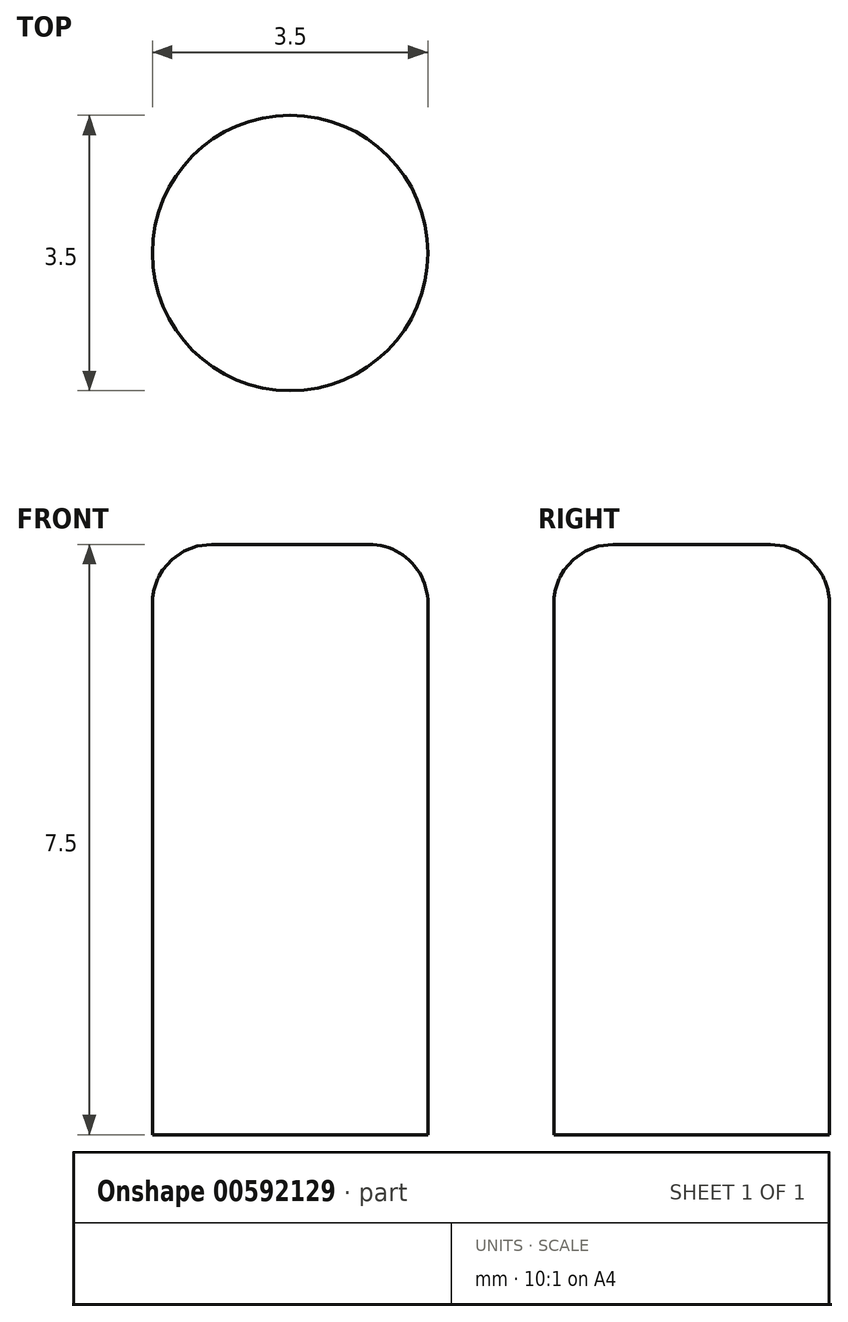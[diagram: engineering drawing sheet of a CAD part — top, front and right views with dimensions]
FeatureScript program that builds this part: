
annotation { "Feature Type Name" : "Feature", "Feature Type Description" : "" }
export const myFeature = defineFeature(function(context is Context, id is Id, definition is map)
    precondition{}
    {
        {
            var Q0;
            Q0=qCreatedBy(makeId("Top.planeOp"),FACE);
            var sketch = newSketch(context, id + "F0", { "sketchPlane" : qUnion([Q0])});
            skCircle(sketch, "E0", {"center": v(0, 0) * mm, "radius": 3.5 * mm});
            skSolve(sketch);
        }
        {
            var Q0;
            Q0 = qSketchRegion(id + "F0", true);
            extrude(context, id + "F1", {"entities" : qUnion([Q0]), "depth" : 15 * mm, "offsetDistance" : 25 * mm});
        }
        {
            var Q0;
            Q0=makeQuery(id+"F1.opExtrude","CAP_EDGE",EDGE,{"disambiguationData":[OSD([sQuery(id+"F0.wireOp",EDGE,"E0")])],"isStart":false});
            fillet(context, id + "F2", {"entities" : qUnion([Q0]), "radius" : 1.5 * mm, "tangentPropagation" : true, "allowEdgeOverflow" : false});
        }
        {
            var Q0;
            Q0=makeQuery(id+"F1.opExtrude","SWEPT_BODY",BODY,{"disambiguationData":[OSD([sQuery(id+"F0.wireOp",EDGE,"E0")])]});
            var Q1;
            Q1=qCreatedBy(makeId("Origin.pointOp"),VERTEX);
            var Q2;
            Q2=qCreatedBy(makeId("Origin.pointOp"),VERTEX);
            transform(context, id + "F3", {"entities" : qUnion([Q0]), "transformType" : TransformType.SCALE_UNIFORMLY, "scale" : .5, "scalePoint" : qUnion([Q2]), "makeCopy" : false});
        }
    });
